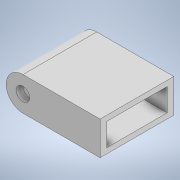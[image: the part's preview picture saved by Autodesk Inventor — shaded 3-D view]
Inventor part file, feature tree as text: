
AUTODESK INVENTOR PART (.ipt)
format: ipt  version: 2022 (Build 260153000, 153)  size: 137,216 bytes
history: native  units: mm
features: extrude x4, sketch x4, other x1, fillet x1
ambient origin geometry x8: Origin, YZ Plane, XZ Plane, XY Plane, X Axis, Y Axis, Z Axis, Center Point
bodies: Solid1 (feature_tree)
feature tree (10):
  extrude  "Extrusion1"  Depth=25.0mm
  extrude  "Extrusion2"  Depth=10.0mm
  extrude  "Extrusion3"  TaperAngle=0.0deg  [1 undecoded]
  other  "Full Round Fillet1"
  fillet  "Fillet1"  Radius=45.0mm
  extrude  "Extrusion4"  Depth=27.5mm
  sketch  "Sketch1"  dims[d0=80.0mm d1=25.0mm]
  sketch  "Sketch2"  dims[d2=55.0mm d3=0.0mm d4=10.0mm]
  sketch  "Sketch3"  dims[d5=12.5mm d6=0.0mm d7=0.0mm d8=45.0mm]
  sketch  "Sketch4"  dims[d9=17.0mm d10=27.5mm d11=12.5mm d12=73.25mm d13=0.0mm d14=12.5mm d15=10.0mm d16=0.0mm]
note: 1 required parameter value undecoded (feature->parameter linkage not recoverable at this tier; creation-order binding heuristic only, values carry confidence <= 0.55)
